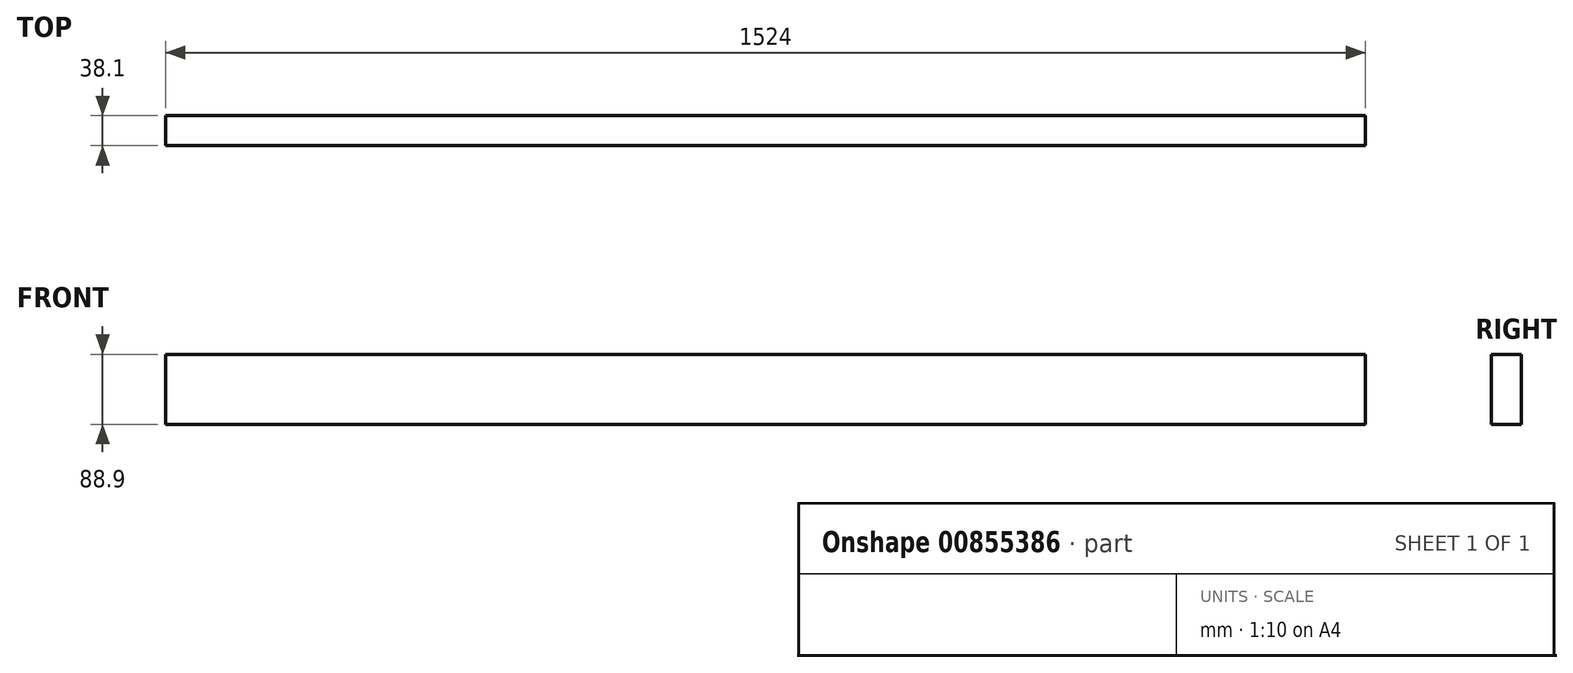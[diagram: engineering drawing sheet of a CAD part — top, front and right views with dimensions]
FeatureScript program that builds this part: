
annotation { "Feature Type Name" : "Feature", "Feature Type Description" : "" }
export const myFeature = defineFeature(function(context is Context, id is Id, definition is map)
    precondition{}
    {
        {
            var Q0;
            Q0=qCreatedBy(makeId("Right.planeOp"),FACE);
            var sketch = newSketch(context, id + "F0", { "sketchPlane" : qUnion([Q0])});
            skLineSegment(sketch, "E0.bottom", {"start": v(0, 0) * mm, "end": v(38.1, 0) * mm});
            skLineSegment(sketch, "E0.top", {"start": v(0, 88.9) * mm, "end": v(38.1, 88.9) * mm});
            skLineSegment(sketch, "E0.left", {"start": v(0, 0) * mm, "end": v(0, 88.9) * mm});
            skLineSegment(sketch, "E0.right", {"start": v(38.1, 0) * mm, "end": v(38.1, 88.9) * mm});
            skSolve(sketch);
        }
        {
            var Q0;
            Q0 = qSketchRegion(id + "F0", true);
            extrude(context, id + "F1", {"entities" : qUnion([Q0]), "depth" : 1524 * mm, "offsetDistance" : 25.4 * mm});
        }
    });
